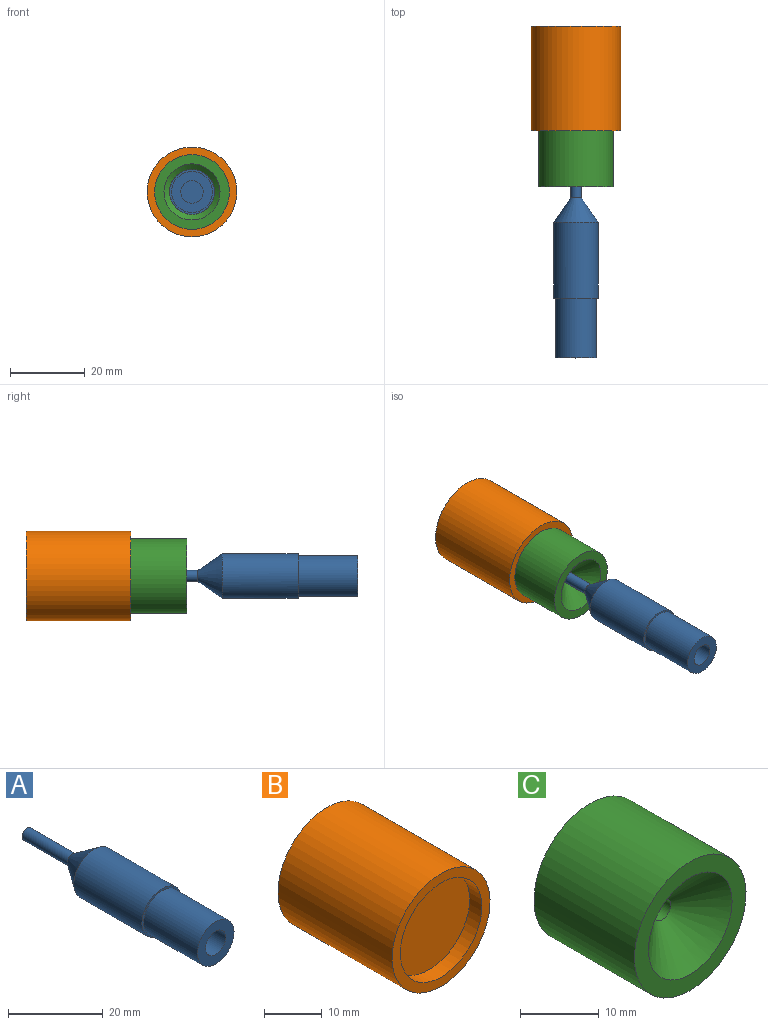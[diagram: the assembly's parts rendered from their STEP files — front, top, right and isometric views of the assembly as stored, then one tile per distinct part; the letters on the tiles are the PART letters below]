
ASSEMBLY  parts=3 mates=2
PART A: 9 faces, bbox 12x56.3x12 mm
  f0: cylinder r=6mm len=20.3mm, axis (0,1,0), area 765.3mm2, adj f2,f6
  f1: cylinder r=5.47mm len=16mm, axis (0,-1,0), area 550.4mm2, adj f2,f5
  f2: plane 12x12mm, normal (0,-1,0), area 18.9mm2, adj f0,f1
  f3: plane 6x6mm, normal (0,-1,0), area 28.3mm2, adj f4
  f4: cylinder r=3mm len=28mm, axis (0,-1,0), area 527.8mm2, adj f3,f5
  f5: plane 10.95x10.95mm, normal (0,-1,0), area 65.9mm2, adj f1,f4
  f6: cone r=1.47mm half-angle=34.8deg, axis (0,-1,0), area 186mm2, adj f0,f8
  f7: plane 2.95x2.95mm, normal (0,1,0), area 6.8mm2, adj f8
  f8: cylinder r=1.47mm len=13.5mm, axis (0,1,0), area 125.1mm2, adj f6,f7
PART B: 9 faces, bbox 24x28x24 mm
  f0: cylinder r=12mm len=28mm, axis (0,1,0), area 2111.2mm2, adj f1,f2
  f1: plane 24x24mm, normal (0,-1,0), area 138.2mm2, adj f0,f3
  f2: plane 24x24mm, normal (0,1,0), area 138.2mm2, adj f0,f5
  f3: cylinder r=10mm len=20mm, axis (0,-1,0), area 188.5mm2, adj f1,f4
  f4: plane 20x20mm, normal (0,-1,0), area 314.2mm2, adj f3
  f5: cylinder r=10mm len=20mm, axis (0,1,0), area 188.5mm2, adj f2,f6
  f6: plane 20x20mm, normal (0,1,0), area 160.2mm2, adj f5,f7
  f7: cylinder r=7mm len=14mm, axis (0,1,0), area 615.8mm2, adj f6,f8
  f8: plane 14x14mm, normal (0,1,0), area 153.9mm2, adj f7
PART C: 5 faces, bbox 20x18x20 mm
  f0: cylinder r=10mm len=20mm, axis (0,1,0), area 1131mm2, adj f1,f2
  f1: plane 20x20mm, normal (0,-1,0), area 137.4mm2, adj f0,f4
  f2: plane 20x20mm, normal (0,1,0), area 307.1mm2, adj f0,f3
  f3: cylinder r=1.5mm len=13mm, axis (0,-1,0), area 122.5mm2, adj f2,f4
  f4: cone r=1.5mm half-angle=50.2deg, axis (0,-1,0), area 220.8mm2, adj f1,f3
PLACE A t=(2.07,-11.89,-1.58)mm
PLACE B t=(2.07,20.61,-1.58)mm
PLACE C t=(2.07,-4.39,-1.58)mm
MATE slider A.f8 <-> C.f3  axis (0,1,0) through (2.07,-18.64,-1.58)mm
MATE fastened B.f3 <-> C.f0  axis (0,-1,0) through (2.07,-4.39,-1.58)mm
